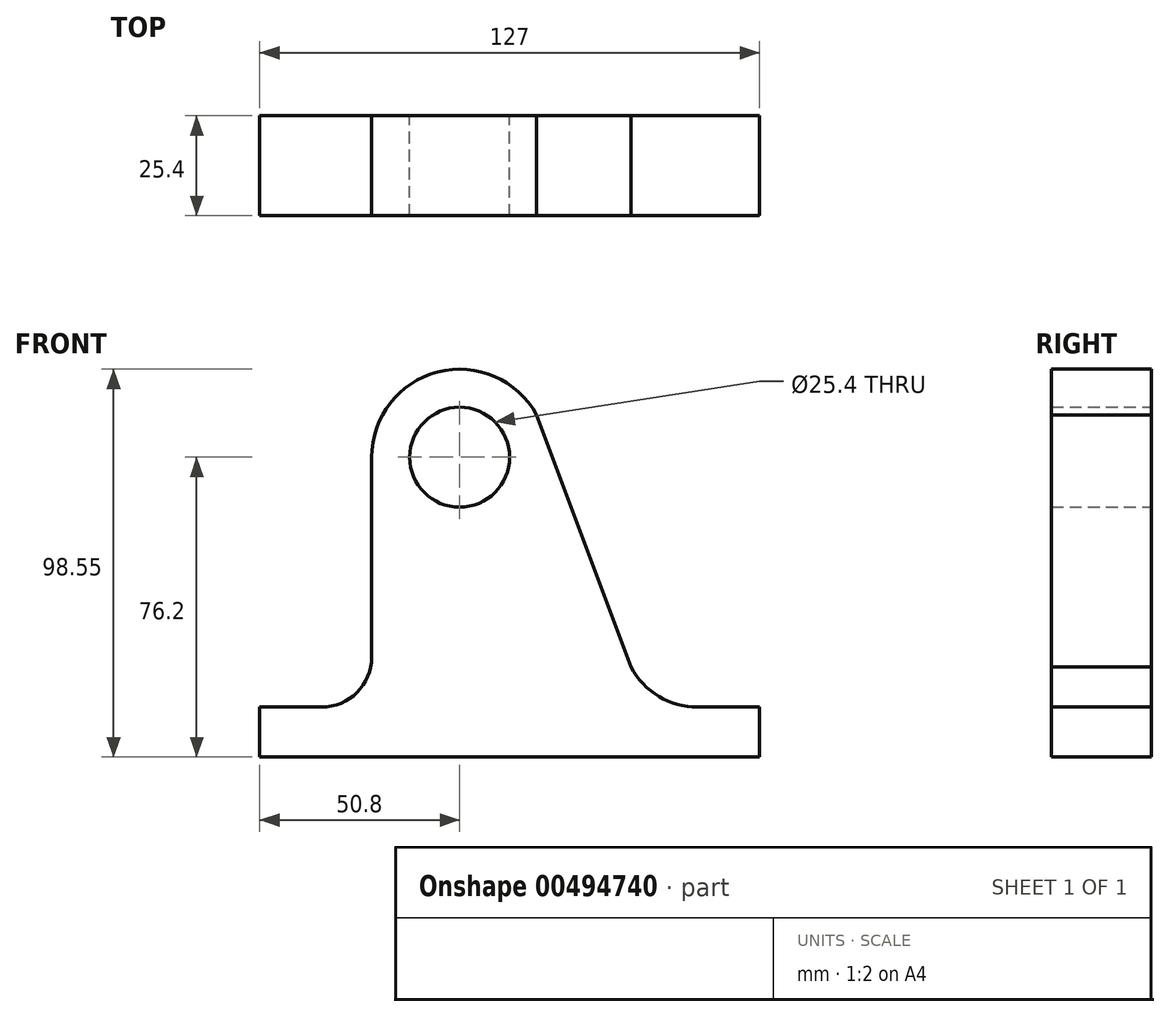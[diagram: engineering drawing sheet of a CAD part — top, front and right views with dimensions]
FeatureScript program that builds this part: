
annotation { "Feature Type Name" : "Feature", "Feature Type Description" : "" }
export const myFeature = defineFeature(function(context is Context, id is Id, definition is map)
    precondition{}
    {
        {
            var Q0;
            Q0=qCreatedBy(makeId("Front.planeOp"),FACE);
            var sketch = newSketch(context, id + "F0", { "sketchPlane" : qUnion([Q0])});
            skCircle(sketch, "E0", {"center": v(0, 0) * mm, "radius": 12.7 * mm});
            skArc(sketch, "E1", {"start": v(19.58, 10.78) * mm, "mid": v(-5.56, 21.65) * mm, "end": v(-22.35, 0) * mm});
            skLineSegment(sketch, "E2", {"start": v(0, -76.2) * mm, "end": v(-50.8, -76.2) * mm});
            skLineSegment(sketch, "E3", {"start": v(-50.8, -76.2) * mm, "end": v(-50.8, -63.5) * mm});
            skLineSegment(sketch, "E4", {"start": v(-22.35, 0) * mm, "end": v(-22.35, -50.8) * mm});
            skLineSegment(sketch, "E5", {"start": v(-35.05, -63.5) * mm, "end": v(-50.8, -63.5) * mm});
            skPoint(sketch, "E6.visualSharp", {"position": v(-22.35, -63.5) * mm});
            skArc(sketch, "E6.filletArc", {"start": v(-35.05, -63.5) * mm, "mid": v(-26.07, -59.78) * mm, "end": v(-22.35, -50.8) * mm});
            skLineSegment(sketch, "E7", {"start": v(0, -76.2) * mm, "end": v(76.2, -76.2) * mm});
            skLineSegment(sketch, "E8", {"start": v(76.2, -76.2) * mm, "end": v(76.2, -63.5) * mm});
            skLineSegment(sketch, "E9", {"start": v(76.2, -63.5) * mm, "end": v(60.45, -63.5) * mm});
            skArc(sketch, "E10", {"start": v(43.57, -53.27) * mm, "mid": v(50.58, -60.74) * mm, "end": v(60.45, -63.5) * mm});
            skLineSegment(sketch, "E11", {"start": v(19.58, 10.78) * mm, "end": v(43.57, -53.27) * mm});
            skSolve(sketch);
        }
        {
            var Q0;
            Q0 = qSketchRegion(id + "F0", true);
            extrude(context, id + "F1", {"entities" : qUnion([Q0]), "depth" : 25.4 * mm});
        }
    });
